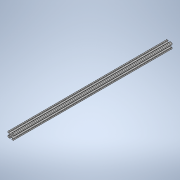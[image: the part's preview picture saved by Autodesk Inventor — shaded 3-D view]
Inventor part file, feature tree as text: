
AUTODESK INVENTOR PART (.ipt)
format: ipt  version: 2020 (Build 240168000, 168)  size: 237,056 bytes
history: native  units: in
note: dims shown in document units (in); Inventor stores cm internally (conversion verified against a paired STEP export)
features: extrude x1, sketch x1
ambient origin geometry x8: Origin, YZ Plane, XZ Plane, XY Plane, X Axis, Y Axis, Z Axis, Center Point
bodies: Solid1 (feature_tree)
feature tree (2):
  extrude  "Extrusion1"  [1 undecoded]
  sketch  "Sketch1"  dims[d0=27.0in d1=0.0in]
note: 1 required parameter value undecoded (feature->parameter linkage not recoverable at this tier; creation-order binding heuristic only, values carry confidence <= 0.55)
